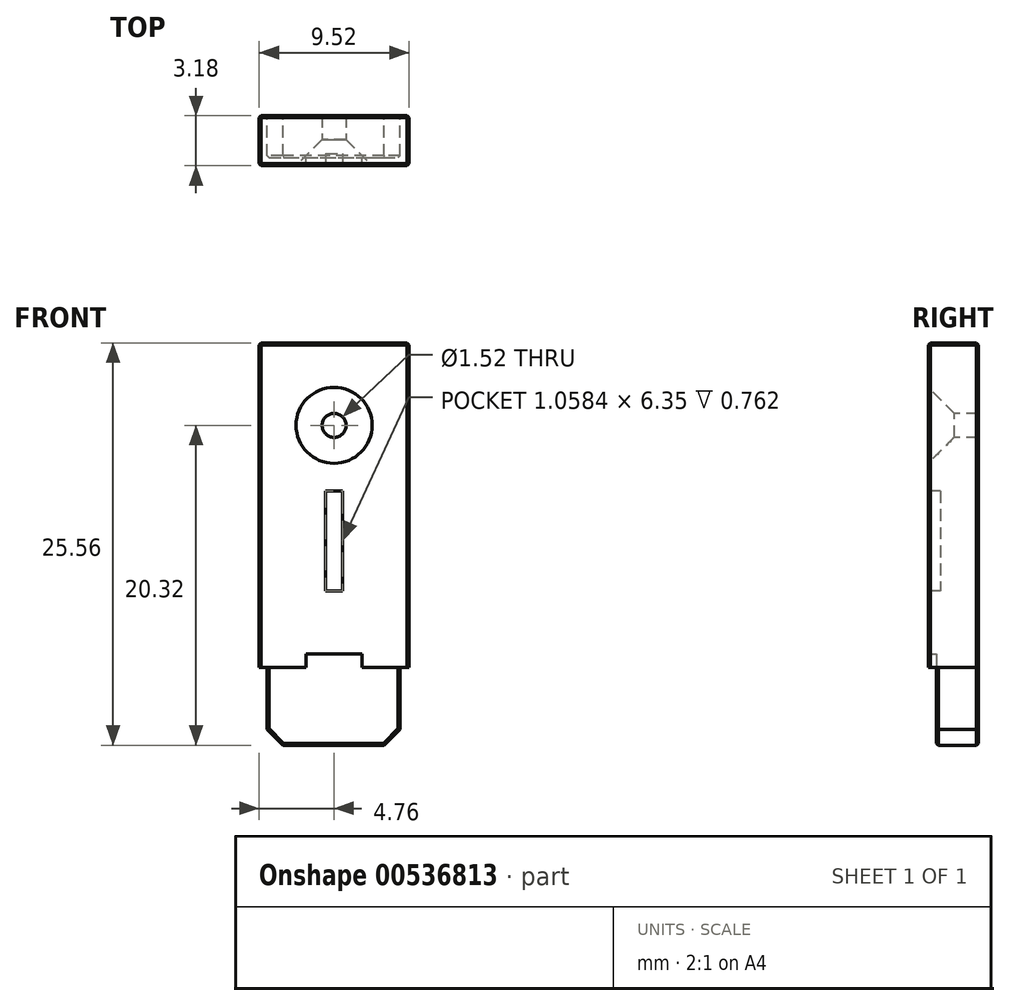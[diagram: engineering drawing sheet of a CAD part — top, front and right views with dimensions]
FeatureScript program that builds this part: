
annotation { "Feature Type Name" : "Feature", "Feature Type Description" : "" }
export const myFeature = defineFeature(function(context is Context, id is Id, definition is map)
    precondition{}
    {
        {
            var Q0;
            Q0=qCreatedBy(makeId("Front.planeOp"),FACE);
            var sketch = newSketch(context, id + "F0", { "sketchPlane" : qUnion([Q0])});
            skLineSegment(sketch, "E0.bottom", {"start": v(-4.76, 5.24) * mm, "end": v(4.76, 5.24) * mm});
            skLineSegment(sketch, "E0.left", {"start": v(-4.76, 5.24) * mm, "end": v(-4.76, -15.38) * mm});
            skLineSegment(sketch, "E1", {"start": v(-4.76, -15.38) * mm, "end": v(-4.76, -15.38) * mm});
            skLineSegment(sketch, "E2", {"start": v(-4.76, -15.38) * mm, "end": v(-1.77, -15.38) * mm});
            skLineSegment(sketch, "E3", {"start": v(4.76, 5.24) * mm, "end": v(4.76, -15.38) * mm});
            skLineSegment(sketch, "E4", {"start": v(1.77, -14.53) * mm, "end": v(1.77, -15.38) * mm});
            skLineSegment(sketch, "E5.MirrorCS", {"start": v(-1.77, -14.53) * mm, "end": v(-1.77, -15.38) * mm});
            skLineSegment(sketch, "E6", {"start": v(1.77, -15.38) * mm, "end": v(1.77, -15.38) * mm});
            skLineSegment(sketch, "E7", {"start": v(1.77, -15.38) * mm, "end": v(4.76, -15.38) * mm});
            skLineSegment(sketch, "E8", {"start": v(-1.77, -14.53) * mm, "end": v(1.77, -14.53) * mm});
            skLineSegment(sketch, "E9", {"start": v(3.19, -20.32) * mm, "end": v(4.2, -19.3) * mm});
            skLineSegment(sketch, "E10", {"start": v(-4.25, -19.3) * mm, "end": v(-3.25, -20.32) * mm});
            skLineSegment(sketch, "E11", {"start": v(-3.25, -20.32) * mm, "end": v(3.19, -20.32) * mm});
            skLineSegment(sketch, "E12", {"start": v(4.2, -19.3) * mm, "end": v(4.2, -19.3) * mm});
            skLineSegment(sketch, "E13", {"start": v(4.2, -19.3) * mm, "end": v(4.2, -15.38) * mm});
            skLineSegment(sketch, "E14", {"start": v(-4.25, -19.3) * mm, "end": v(-4.25, -15.38) * mm});
            skSolve(sketch);
        }
        {
            var Q0;
            Q0=makeQuery(id+"F0.imprint","IMPRINT",FACE,{"disambiguationData":[TD([[makeQuery(id+"F0.imprint","IMPRINT",EDGE,{"derivedFrom":sQuery(id+"F0.wireOp",EDGE,"E0.bottom")}),-1.0]])]});
            extrude(context, id + "F1", {"entities" : qUnion([Q0]), "depth" : 3.17 * mm, "offsetDistance" : 25.4 * mm});
        }
        {
            var Q0;
            Q0=makeQuery(id+"F1.opExtrude","CAP_FACE",FACE,{"disambiguationData":[OSD([sQuery(id+"F0.wireOp",EDGE,"E0.bottom"),sQuery(id+"F0.wireOp",EDGE,"E0.left"),sQuery(id+"F0.wireOp",EDGE,"E2"),sQuery(id+"F0.wireOp",EDGE,"E3"),sQuery(id+"F0.wireOp",EDGE,"E4"),sQuery(id+"F0.wireOp",EDGE,"E5.MirrorCS"),sQuery(id+"F0.wireOp",EDGE,"E7"),sQuery(id+"F0.wireOp",EDGE,"E8")])],"isStart":false});
            var sketch = newSketch(context, id + "F2", { "sketchPlane" : qUnion([Q0])});
            skPoint(sketch, "E15", {"position": v(0, 0) * mm});
            skSolve(sketch);
        }
        {
            var Q0;
            {var subQ1=sQuery(id+"F0.wireOp",EDGE,"E4");Q0=makeQuery(id+"F0.imprint","IMPRINT",FACE,{"disambiguationData":[TD([[makeQuery(id+"F0.imprint","IMPRINT",EDGE,{"derivedFrom":subQ1}),-1.0]])]});}
            extrude(context, id + "F3", {"entities" : qUnion([Q0]), "operationType" : NewBodyOperationType.ADD, "depth" : 2.67 * mm, "offsetDistance" : 25.4 * mm});
        }
        {
            var Q0;
            Q0=makeQuery(id+"F1.opExtrude","CAP_EDGE",EDGE,{"disambiguationData":[OSD([sQuery(id+"F0.wireOp",EDGE,"E0.bottom")])],"isStart":false});
            var Q1;
            Q1=makeQuery(id+"F1.opExtrude","CAP_EDGE",EDGE,{"disambiguationData":[OSD([sQuery(id+"F0.wireOp",EDGE,"E0.left")])],"isStart":false});
            var Q2;
            Q2=makeQuery(id+"F1.opExtrude","SWEPT_EDGE",EDGE,{"disambiguationData":[OSD([sQuery(id+"F0.wireOp",EDGE,"E0.bottom"),sQuery(id+"F0.wireOp",EDGE,"E0.left")])]});
            var Q3;
            Q3=makeQuery(id+"F1.opExtrude","CAP_EDGE",EDGE,{"disambiguationData":[OSD([sQuery(id+"F0.wireOp",EDGE,"E0.left")])],"isStart":true});
            var Q4;
            Q4=makeQuery(id+"F1.opExtrude","CAP_EDGE",EDGE,{"disambiguationData":[OSD([sQuery(id+"F0.wireOp",EDGE,"E3")])],"isStart":false});
            var Q5;
            Q5=makeQuery(id+"F1.opExtrude","CAP_EDGE",EDGE,{"disambiguationData":[OSD([sQuery(id+"F0.wireOp",EDGE,"E3")])],"isStart":true});
            var Q6;
            Q6=makeQuery(id+"F1.opExtrude","SWEPT_EDGE",EDGE,{"disambiguationData":[OSD([sQuery(id+"F0.wireOp",EDGE,"E0.bottom"),sQuery(id+"F0.wireOp",EDGE,"E3")])]});
            var Q7;
            Q7=makeQuery(id+"F1.opExtrude","CAP_EDGE",EDGE,{"disambiguationData":[OSD([sQuery(id+"F0.wireOp",EDGE,"E0.bottom")])],"isStart":true});
            var Q8;
            Q8=makeQuery(id+"F3.opExtrude","CAP_EDGE",EDGE,{"disambiguationData":[OSD([sQuery(id+"F0.wireOp",EDGE,"E14")])],"isStart":false});
            var Q9;
            Q9=makeQuery(id+"F3.opExtrude","CAP_EDGE",EDGE,{"disambiguationData":[OSD([sQuery(id+"F0.wireOp",EDGE,"E13")])],"isStart":false});
            var Q10;
            Q10=makeQuery(id+"F3.opExtrude","CAP_EDGE",EDGE,{"disambiguationData":[OSD([sQuery(id+"F0.wireOp",EDGE,"E13")])],"isStart":true});
            var Q11;
            Q11=makeQuery(id+"F3.opExtrude","CAP_EDGE",EDGE,{"disambiguationData":[OSD([sQuery(id+"F0.wireOp",EDGE,"E14")])],"isStart":true});
            var Q12;
            Q12=makeQuery(id+"F3.opExtrude","CAP_EDGE",EDGE,{"disambiguationData":[OSD([sQuery(id+"F0.wireOp",EDGE,"E9")])],"isStart":false});
            var Q13;
            Q13=makeQuery(id+"F3.opExtrude","CAP_EDGE",EDGE,{"disambiguationData":[OSD([sQuery(id+"F0.wireOp",EDGE,"E11")])],"isStart":false});
            var Q14;
            Q14=makeQuery(id+"F3.opExtrude","CAP_EDGE",EDGE,{"disambiguationData":[OSD([sQuery(id+"F0.wireOp",EDGE,"E10")])],"isStart":false});
            var Q15;
            Q15=makeQuery(id+"F3.opExtrude","CAP_EDGE",EDGE,{"disambiguationData":[OSD([sQuery(id+"F0.wireOp",EDGE,"E10")])],"isStart":true});
            var Q16;
            Q16=makeQuery(id+"F3.opExtrude","CAP_EDGE",EDGE,{"disambiguationData":[OSD([sQuery(id+"F0.wireOp",EDGE,"E11")])],"isStart":true});
            var Q17;
            Q17=makeQuery(id+"F3.opExtrude","CAP_EDGE",EDGE,{"disambiguationData":[OSD([sQuery(id+"F0.wireOp",EDGE,"E9")])],"isStart":true});
            chamfer(context, id + "F4", {"entities" : qUnion([Q0, Q1, Q2, Q3, Q4, Q5, Q6, Q7, Q8, Q9, Q10, Q11, Q12, Q13, Q14, Q15, Q16, Q17]), "width" : 0.13 * mm, "tangentPropagation" : true});
        }
        {
            var Q0;
            Q0=sQuery(id+"F2.wireOp",VERTEX,"E15");
            var Q1;
            Q1=makeQuery(id+"F1.opExtrude","SWEPT_BODY",BODY,{"disambiguationData":[OSD([sQuery(id+"F0.wireOp",EDGE,"E0.bottom"),sQuery(id+"F0.wireOp",EDGE,"E0.left"),sQuery(id+"F0.wireOp",EDGE,"E2"),sQuery(id+"F0.wireOp",EDGE,"E3"),sQuery(id+"F0.wireOp",EDGE,"E4"),sQuery(id+"F0.wireOp",EDGE,"E5.MirrorCS"),sQuery(id+"F0.wireOp",EDGE,"E7"),sQuery(id+"F0.wireOp",EDGE,"E8")])]});
            hole(context, id + "F5", {"style" : HoleStyle.C_SINK, "endStyle" : HoleEndStyle.THROUGH, "holeDiameter" : 1.52 * mm, "cSinkDiameter" : 4.83 * mm, "cSinkAngle" : 90 * degree, "isTappedThrough" : true, "tappedDepth" : 12.7 * mm, "tapClearance" : 3, "startFromSketch" : true, "locations" : qUnion([Q0]), "scope" : qUnion([Q1])});
        }
        {
            var Q0;
            Q0=makeQuery(id+"F1.opExtrude","CAP_FACE",FACE,{"disambiguationData":[OSD([sQuery(id+"F0.wireOp",EDGE,"E0.bottom"),sQuery(id+"F0.wireOp",EDGE,"E0.left"),sQuery(id+"F0.wireOp",EDGE,"E2"),sQuery(id+"F0.wireOp",EDGE,"E3"),sQuery(id+"F0.wireOp",EDGE,"E4"),sQuery(id+"F0.wireOp",EDGE,"E5.MirrorCS"),sQuery(id+"F0.wireOp",EDGE,"E7"),sQuery(id+"F0.wireOp",EDGE,"E8")])],"isStart":false});
            var sketch = newSketch(context, id + "F6", { "sketchPlane" : qUnion([Q0])});
            skLineSegment(sketch, "E16", {"start": v(-0.53, -4.18) * mm, "end": v(-0.53, -10.53) * mm});
            skLineSegment(sketch, "E17.MirrorCS", {"start": v(0.53, -4.18) * mm, "end": v(0.53, -10.53) * mm});
            skLineSegment(sketch, "E18", {"start": v(-0.53, -4.18) * mm, "end": v(0.53, -4.18) * mm});
            skLineSegment(sketch, "E19", {"start": v(-0.53, -10.53) * mm, "end": v(0.53, -10.53) * mm});
            skSolve(sketch);
        }
        {
            var Q0;
            Q0=makeQuery(id+"F6.imprint","IMPRINT",FACE,{"disambiguationData":[TD([[makeQuery(id+"F6.imprint","IMPRINT",EDGE,{"derivedFrom":sQuery(id+"F6.wireOp",EDGE,"E16")}),1.0]])]});
            extrude(context, id + "F7", {"entities" : qUnion([Q0]), "operationType" : NewBodyOperationType.REMOVE, "oppositeDirection" : true, "depth" : 0.76 * mm, "offsetDistance" : 25.4 * mm});
        }
    });
